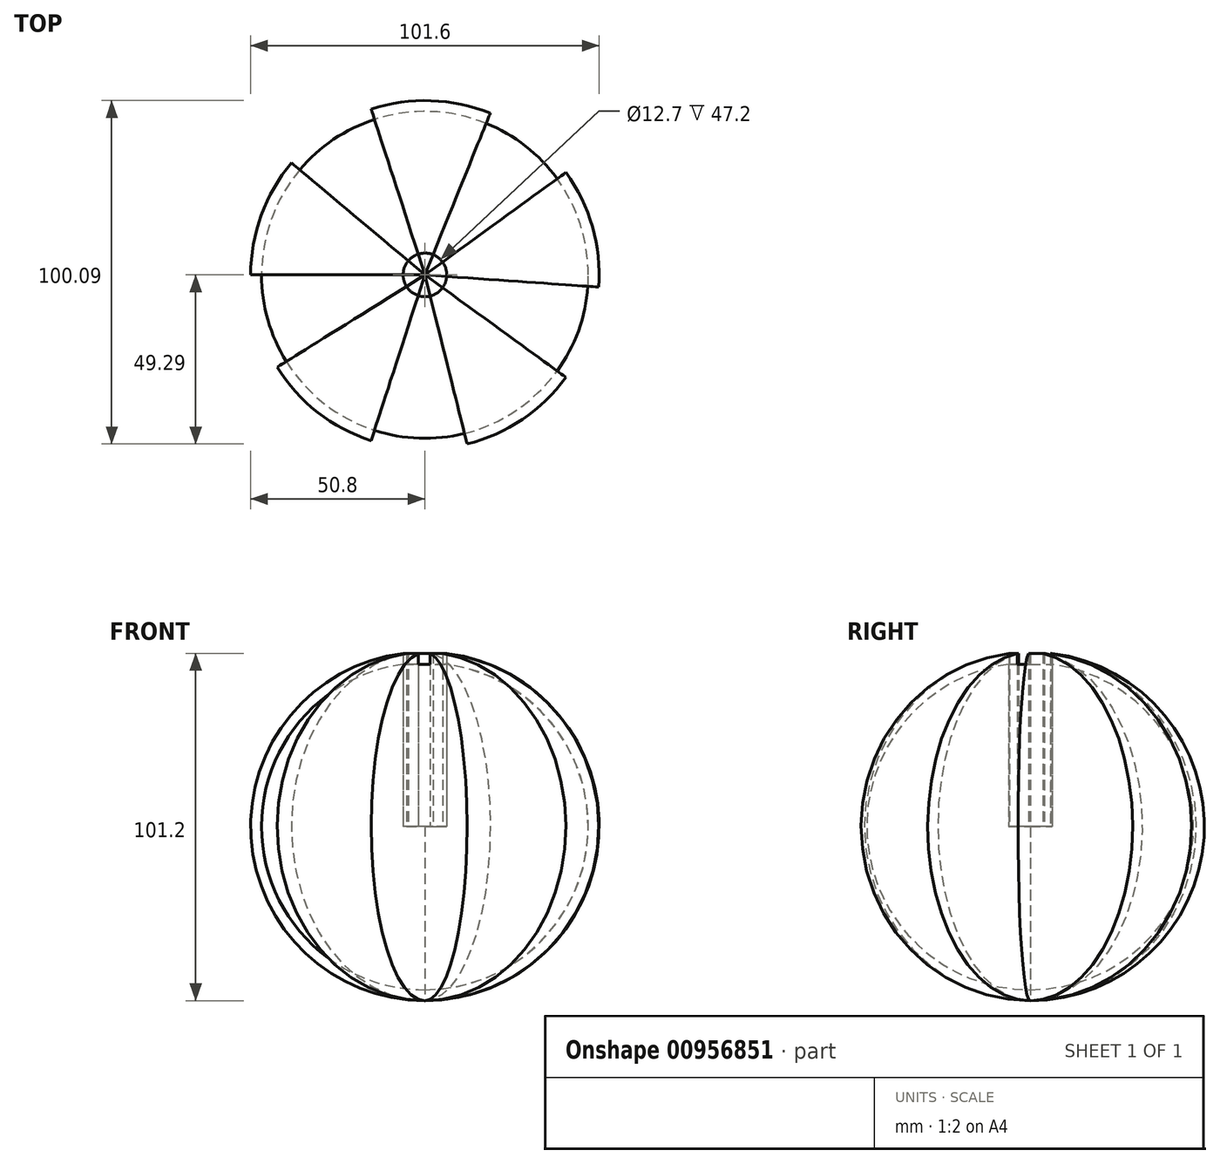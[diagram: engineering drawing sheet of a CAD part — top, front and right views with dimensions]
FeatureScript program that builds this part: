
annotation { "Feature Type Name" : "Feature", "Feature Type Description" : "" }
export const myFeature = defineFeature(function(context is Context, id is Id, definition is map)
    precondition{}
    {
        {
            var Q0;
            Q0=qCreatedBy(makeId("Front.planeOp"),FACE);
            var sketch = newSketch(context, id + "F0", { "sketchPlane" : qUnion([Q0])});
            skArc(sketch, "E0", {"start": v(0, 50.8) * mm, "mid": v(-50.8, 0) * mm, "end": v(0, -50.8) * mm});
            skLineSegment(sketch, "E1", {"start": v(0, 50.8) * mm, "end": v(0, -50.8) * mm});
            skSolve(sketch);
        }
        {
            var Q0;
            Q0 = qSketchRegion(id + "F0", true);
            var Q1;
            Q1=sQuery(id+"F0.wireOp",EDGE,"E1");
            revolve(context, id + "F1", {"surfaceOperationType" : NewSurfaceOperationType.NEW, "entities" : qUnion([Q0]), "axis" : qUnion([Q1]), "revolveType" : RevolveType.ONE_DIRECTION, "angle" : 40 * degree});
        }
        {
            var Q0;
            Q0=makeQuery(id+"F1.opRevolve","SWEPT_BODY",BODY,{"disambiguationData":[OSD([sQuery(id+"F0.wireOp",EDGE,"E0"),sQuery(id+"F0.wireOp",EDGE,"E1")])]});
            var Q1;
            Q1=makeQuery(id+"F1.opRevolve","CAP_EDGE",EDGE,{"disambiguationData":[OSD([sQuery(id+"F0.wireOp",EDGE,"E1")])],"isStart":true});
            circularPattern(context, id + "F2", {"entities" : qUnion([Q0]), "axis" : qUnion([Q1]), "angle" : 360 * degree, "instanceCount" : 5, "equalSpace" : true});
        }
        {
            var Q0;
            Q0=makeQuery(id+"F1.opRevolve","CAP_FACE",FACE,{"disambiguationData":[OSD([sQuery(id+"F0.wireOp",EDGE,"E0"),sQuery(id+"F0.wireOp",EDGE,"E1")])],"isStart":true});
            var sketch = newSketch(context, id + "F3", { "sketchPlane" : qUnion([Q0])});
            skArc(sketch, "E2", {"start": v(0, 47.63) * mm, "mid": v(-47.63, 0) * mm, "end": v(0, -47.63) * mm});
            skLineSegment(sketch, "E3", {"start": v(0, 47.62) * mm, "end": v(0, -47.62) * mm});
            skSolve(sketch);
        }
        {
            var Q0;
            Q0 = qSketchRegion(id + "F3", true);
            var Q1;
            Q1=sQuery(id+"F3.wireOp",EDGE,"E3");
            revolve(context, id + "F4", {"surfaceOperationType" : NewSurfaceOperationType.NEW, "entities" : qUnion([Q0]), "axis" : qUnion([Q1]), "revolveType" : RevolveType.FULL});
        }
        {
            var Q0;
            Q0=qCreatedBy(makeId("Top.planeOp"),FACE);
            var sketch = newSketch(context, id + "F5", { "sketchPlane" : qUnion([Q0])});
            skCircle(sketch, "E4", {"center": v(0, 0) * mm, "radius": 6.35 * mm});
            skSolve(sketch);
        }
        {
            var Q0;
            Q0 = qSketchRegion(id + "F5", true);
            extrude(context, id + "F6", {"entities" : qUnion([Q0]), "operationType" : NewBodyOperationType.REMOVE, "depth" : 50.8 * mm, "offsetDistance" : 25.4 * mm});
        }
    });
